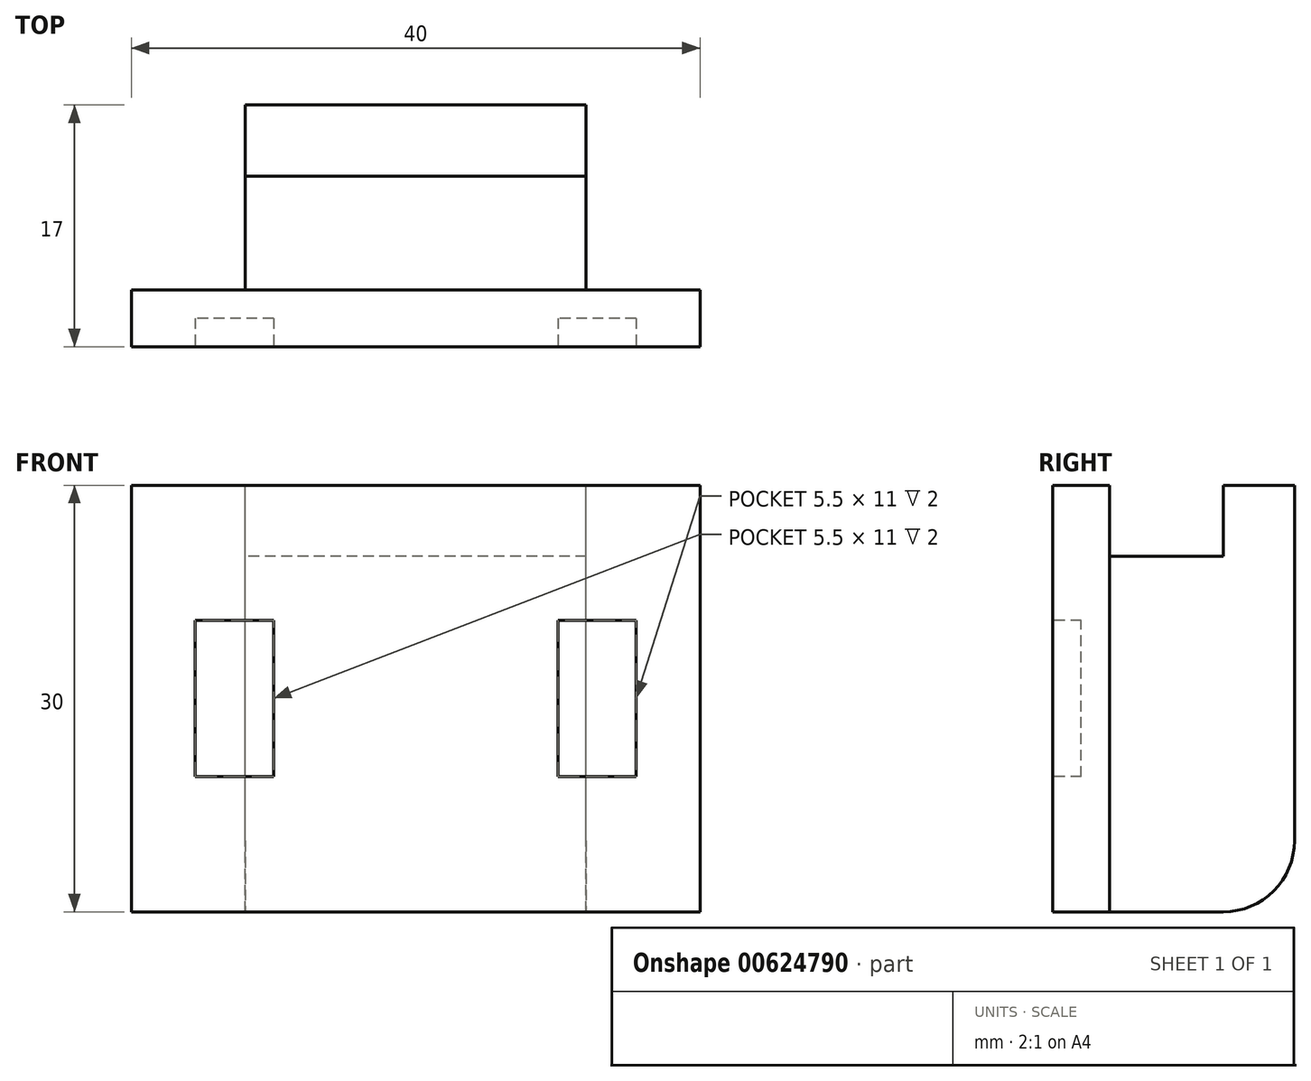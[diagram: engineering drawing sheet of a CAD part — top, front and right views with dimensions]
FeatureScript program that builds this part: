
annotation { "Feature Type Name" : "Feature", "Feature Type Description" : "" }
export const myFeature = defineFeature(function(context is Context, id is Id, definition is map)
    precondition{}
    {
        {
            var Q0;
            Q0=qCreatedBy(makeId("Front.planeOp"),FACE);
            var sketch = newSketch(context, id + "F0", { "sketchPlane" : qUnion([Q0])});
            skLineSegment(sketch, "E0.bottom", {"start": v(12, -15) * mm, "end": v(-12, -15) * mm});
            skLineSegment(sketch, "E0.top", {"start": v(12, 15) * mm, "end": v(-12, 15) * mm});
            skLineSegment(sketch, "E0.left", {"start": v(12, -15) * mm, "end": v(12, 15) * mm});
            skLineSegment(sketch, "E0.right", {"start": v(-12, -15) * mm, "end": v(-12, 15) * mm});
            skPoint(sketch, "E0.middle", {"position": v(0, 0) * mm});
            skSolve(sketch);
        }
        {
            var Q0;
            Q0 = qSketchRegion(id + "F0", true);
            extrude(context, id + "F1", {"entities" : qUnion([Q0]), "depth" : 5 * mm, "offsetDistance" : 25 * mm});
        }
        {
            var Q0;
            Q0=makeQuery(id+"F1.opExtrude","CAP_FACE",FACE,{"disambiguationData":[OSD([sQuery(id+"F0.wireOp",EDGE,"E0.bottom"),sQuery(id+"F0.wireOp",EDGE,"E0.top"),sQuery(id+"F0.wireOp",EDGE,"E0.left"),sQuery(id+"F0.wireOp",EDGE,"E0.right")])],"isStart":false});
            var sketch = newSketch(context, id + "F2", { "sketchPlane" : qUnion([Q0])});
            skLineSegment(sketch, "E1.bottom", {"start": v(12, -15) * mm, "end": v(-12, -15) * mm});
            skLineSegment(sketch, "E1.top", {"start": v(12, 10) * mm, "end": v(-12, 10) * mm});
            skLineSegment(sketch, "E1.left", {"start": v(12, -15) * mm, "end": v(12, 10) * mm});
            skLineSegment(sketch, "E1.right", {"start": v(-12, -15) * mm, "end": v(-12, 10) * mm});
            skPoint(sketch, "E1.middle", {"position": v(0, -2.5) * mm});
            skSolve(sketch);
        }
        {
            var Q0;
            Q0 = qSketchRegion(id + "F2", true);
            extrude(context, id + "F3", {"entities" : qUnion([Q0]), "operationType" : NewBodyOperationType.ADD, "depth" : 8 * mm, "offsetDistance" : 25 * mm});
        }
        {
            var Q0;
            Q0=makeQuery(id+"F1.opExtrude","CAP_EDGE",EDGE,{"disambiguationData":[OSD([sQuery(id+"F0.wireOp",EDGE,"E0.bottom")])],"isStart":true});
            fillet(context, id + "F4", {"entities" : qUnion([Q0]), "radius" : 5 * mm, "tangentPropagation" : true, "allowEdgeOverflow" : false});
        }
        {
            var Q0;
            Q0=makeQuery(id+"F3.opExtrude","CAP_FACE",FACE,{"disambiguationData":[OSD([sQuery(id+"F2.wireOp",EDGE,"E1.bottom"),sQuery(id+"F2.wireOp",EDGE,"E1.top"),sQuery(id+"F2.wireOp",EDGE,"E1.left"),sQuery(id+"F2.wireOp",EDGE,"E1.right")])],"isStart":false});
            var sketch = newSketch(context, id + "F5", { "sketchPlane" : qUnion([Q0])});
            skLineSegment(sketch, "E2.bottom", {"start": v(20, -15) * mm, "end": v(-20, -15) * mm});
            skLineSegment(sketch, "E2.top", {"start": v(20, 15) * mm, "end": v(-20, 15) * mm});
            skLineSegment(sketch, "E2.left", {"start": v(20, -15) * mm, "end": v(20, 15) * mm});
            skLineSegment(sketch, "E2.right", {"start": v(-20, -15) * mm, "end": v(-20, 15) * mm});
            skPoint(sketch, "E2.middle", {"position": v(0, 0) * mm});
            skSolve(sketch);
        }
        {
            var Q0;
            Q0 = qSketchRegion(id + "F5", true);
            extrude(context, id + "F6", {"entities" : qUnion([Q0]), "operationType" : NewBodyOperationType.ADD, "depth" : 4 * mm, "offsetDistance" : 25 * mm});
        }
        {
            var Q0;
            Q0=makeQuery(id+"F6.opExtrude","CAP_FACE",FACE,{"disambiguationData":[OSD([sQuery(id+"F5.wireOp",EDGE,"E2.bottom"),sQuery(id+"F5.wireOp",EDGE,"E2.top"),sQuery(id+"F5.wireOp",EDGE,"E2.left"),sQuery(id+"F5.wireOp",EDGE,"E2.right")])],"isStart":false});
            var sketch = newSketch(context, id + "F7", { "sketchPlane" : qUnion([Q0])});
            skLineSegment(sketch, "E3.bottom", {"start": v(-10, -5.5) * mm, "end": v(-15.5, -5.5) * mm});
            skLineSegment(sketch, "E3.top", {"start": v(-10, 5.5) * mm, "end": v(-15.5, 5.5) * mm});
            skLineSegment(sketch, "E3.left", {"start": v(-10, -5.5) * mm, "end": v(-10, 5.5) * mm});
            skLineSegment(sketch, "E3.right", {"start": v(-15.5, -5.5) * mm, "end": v(-15.5, 5.5) * mm});
            skPoint(sketch, "E3.middle", {"position": v(-12.75, 0) * mm});
            skLineSegment(sketch, "E4.bottom", {"start": v(15.5, -5.5) * mm, "end": v(10, -5.5) * mm});
            skLineSegment(sketch, "E4.top", {"start": v(15.5, 5.5) * mm, "end": v(10, 5.5) * mm});
            skLineSegment(sketch, "E4.left", {"start": v(15.5, -5.5) * mm, "end": v(15.5, 5.5) * mm});
            skLineSegment(sketch, "E4.right", {"start": v(10, -5.5) * mm, "end": v(10, 5.5) * mm});
            skPoint(sketch, "E4.middle", {"position": v(12.75, 0) * mm});
            skSolve(sketch);
        }
        {
            var Q0;
            Q0 = qSketchRegion(id + "F7", true);
            extrude(context, id + "F8", {"entities" : qUnion([Q0]), "operationType" : NewBodyOperationType.REMOVE, "oppositeDirection" : true, "depth" : 2 * mm, "offsetDistance" : 25 * mm});
        }
    });
